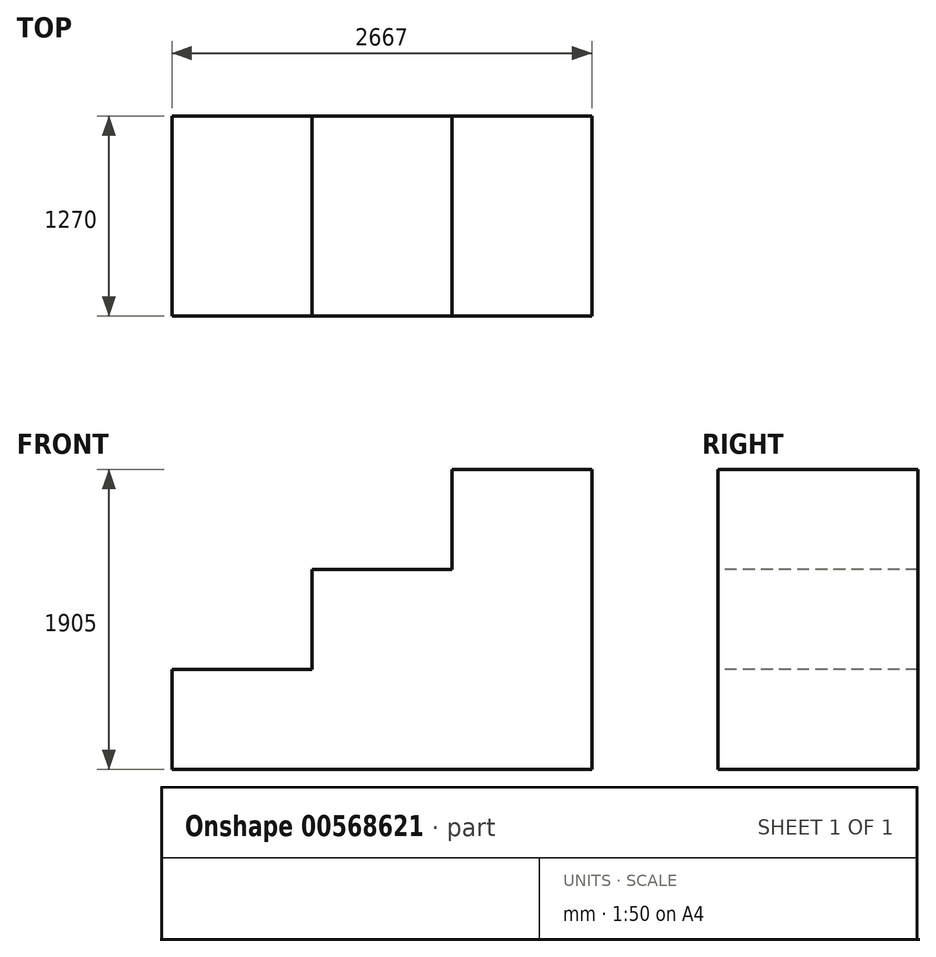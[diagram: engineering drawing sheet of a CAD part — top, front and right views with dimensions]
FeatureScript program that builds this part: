
annotation { "Feature Type Name" : "Feature", "Feature Type Description" : "" }
export const myFeature = defineFeature(function(context is Context, id is Id, definition is map)
    precondition{}
    {
        {
            var Q0;
            Q0=qCreatedBy(makeId("Front.planeOp"),FACE);
            var sketch = newSketch(context, id + "F0", { "sketchPlane" : qUnion([Q0])});
            skLineSegment(sketch, "E0.bottom", {"start": v(0, 0) * mm, "end": v(2667, 0) * mm});
            skLineSegment(sketch, "E0.top", {"start": v(0, 1905) * mm, "end": v(2667, 1905) * mm});
            skLineSegment(sketch, "E0.left", {"start": v(0, 0) * mm, "end": v(0, 1905) * mm});
            skLineSegment(sketch, "E0.right", {"start": v(2667, 0) * mm, "end": v(2667, 1905) * mm});
            skSolve(sketch);
        }
        {
            var Q0;
            Q0=makeQuery(id+"F0.imprint","IMPRINT",FACE,{"disambiguationData":[TD([[makeQuery(id+"F0.imprint","IMPRINT",EDGE,{"derivedFrom":sQuery(id+"F0.wireOp",EDGE,"E0.bottom")}),1.0]])]});
            extrude(context, id + "F1", {"entities" : qUnion([Q0]), "depth" : 1270 * mm, "offsetDistance" : 25.4 * mm});
        }
        {
            var Q0;
            Q0=makeQuery(id+"F1.opExtrude","CAP_FACE",FACE,{"disambiguationData":[OSD([sQuery(id+"F0.wireOp",EDGE,"E0.bottom"),sQuery(id+"F0.wireOp",EDGE,"E0.top"),sQuery(id+"F0.wireOp",EDGE,"E0.left"),sQuery(id+"F0.wireOp",EDGE,"E0.right")])],"isStart":false});
            var sketch = newSketch(context, id + "F2", { "sketchPlane" : qUnion([Q0])});
            skLineSegment(sketch, "E1.bottom", {"start": v(0, 1905) * mm, "end": v(889, 1905) * mm});
            skLineSegment(sketch, "E1.top", {"start": v(0, 635) * mm, "end": v(889, 635) * mm});
            skLineSegment(sketch, "E1.left", {"start": v(0, 1905) * mm, "end": v(0, 635) * mm});
            skLineSegment(sketch, "E1.right", {"start": v(889, 1905) * mm, "end": v(889, 635) * mm});
            skSolve(sketch);
        }
        {
            var Q0;
            Q0=makeQuery(id+"F2.imprint","IMPRINT",FACE,{"disambiguationData":[TD([[makeQuery(id+"F2.imprint","IMPRINT",EDGE,{"derivedFrom":sQuery(id+"F2.wireOp",EDGE,"E1.bottom")}),-1.0]])]});
            extrude(context, id + "F3", {"entities" : qUnion([Q0]), "operationType" : NewBodyOperationType.REMOVE, "endBound" : BoundingType.THROUGH_ALL, "oppositeDirection" : true, "depth" : 25.4 * mm, "offsetDistance" : 25.4 * mm});
        }
        {
            var Q0;
            Q0=makeQuery(id+"F1.opExtrude","CAP_FACE",FACE,{"disambiguationData":[OSD([sQuery(id+"F0.wireOp",EDGE,"E0.bottom"),sQuery(id+"F0.wireOp",EDGE,"E0.top"),sQuery(id+"F0.wireOp",EDGE,"E0.left"),sQuery(id+"F0.wireOp",EDGE,"E0.right")])],"isStart":false});
            var sketch = newSketch(context, id + "F4", { "sketchPlane" : qUnion([Q0])});
            skLineSegment(sketch, "E2.bottom", {"start": v(889, 1905) * mm, "end": v(1778, 1905) * mm});
            skLineSegment(sketch, "E2.top", {"start": v(889, 1270) * mm, "end": v(1778, 1270) * mm});
            skLineSegment(sketch, "E2.left", {"start": v(889, 1905) * mm, "end": v(889, 1270) * mm});
            skLineSegment(sketch, "E2.right", {"start": v(1778, 1905) * mm, "end": v(1778, 1270) * mm});
            skSolve(sketch);
        }
        {
            var Q0;
            Q0=makeQuery(id+"F4.imprint","IMPRINT",FACE,{"disambiguationData":[TD([[makeQuery(id+"F4.imprint","IMPRINT",EDGE,{"derivedFrom":sQuery(id+"F4.wireOp",EDGE,"E2.bottom")}),-1.0]])]});
            extrude(context, id + "F5", {"entities" : qUnion([Q0]), "operationType" : NewBodyOperationType.REMOVE, "endBound" : BoundingType.THROUGH_ALL, "oppositeDirection" : true, "depth" : 25.4 * mm, "offsetDistance" : 25.4 * mm});
        }
    });
